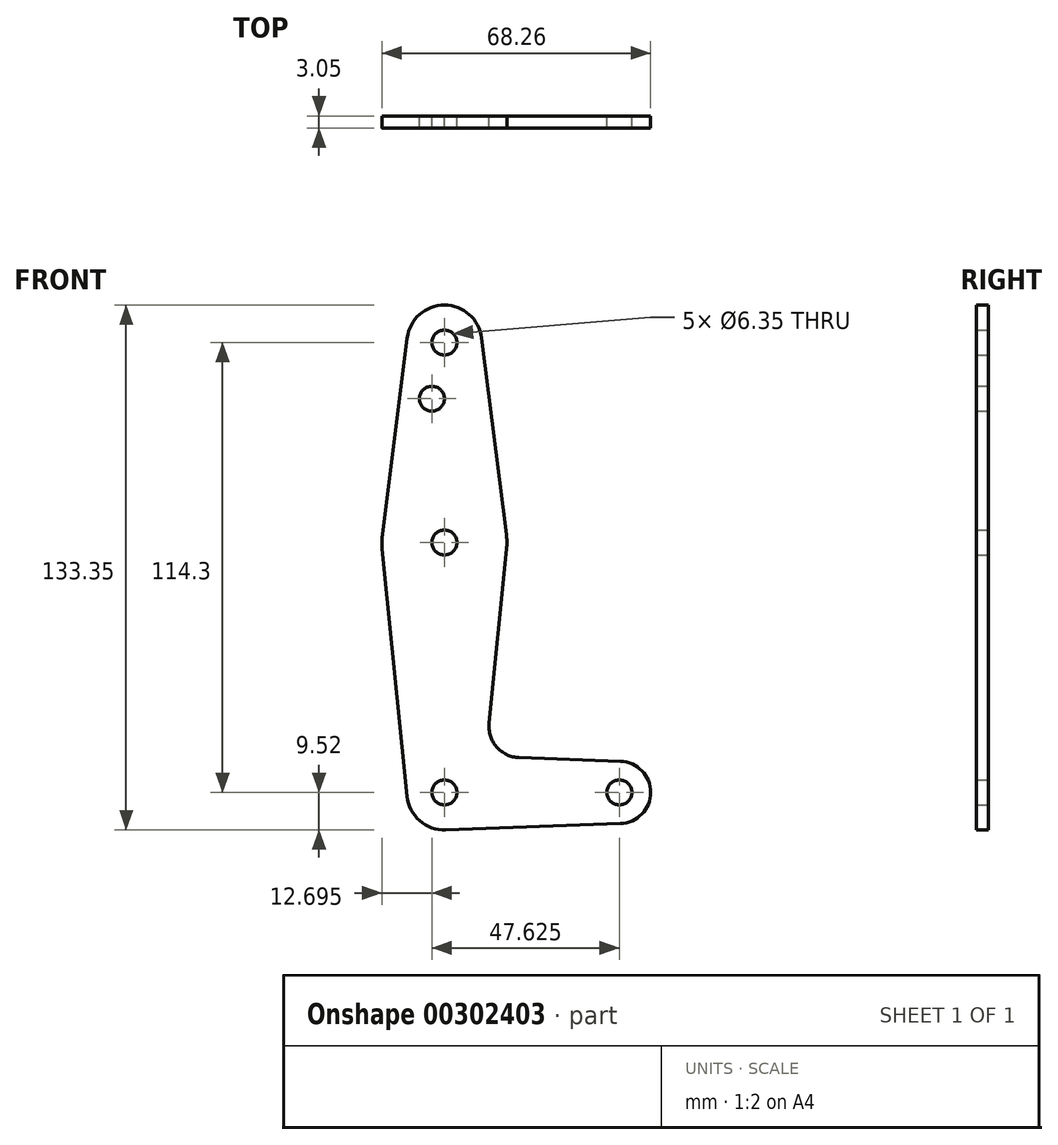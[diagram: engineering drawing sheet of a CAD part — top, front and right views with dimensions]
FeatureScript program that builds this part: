
annotation { "Feature Type Name" : "Feature", "Feature Type Description" : "" }
export const myFeature = defineFeature(function(context is Context, id is Id, definition is map)
    precondition{}
    {
        {
            var Q0;
            Q0=qCreatedBy(makeId("Front.planeOp"),FACE);
            var sketch = newSketch(context, id + "F0", { "sketchPlane" : qUnion([Q0])});
            skLineSegment(sketch, "E0", {"start": v(0, 0) * mm, "end": v(0, 114.3) * mm, "construction": true});
            skLineSegment(sketch, "E1", {"start": v(0, 0) * mm, "end": v(44.45, 0) * mm, "construction": true});
            skCircle(sketch, "E2", {"center": v(0, 114.3) * mm, "radius": 9.53 * mm});
            skCircle(sketch, "E3", {"center": v(0, 63.5) * mm, "radius": 15.88 * mm});
            skCircle(sketch, "E4", {"center": v(0, 0) * mm, "radius": 9.53 * mm});
            skCircle(sketch, "E5", {"center": v(44.45, 0) * mm, "radius": 7.94 * mm});
            skLineSegment(sketch, "E6", {"start": v(9.45, 115.5) * mm, "end": v(15.75, 65.48) * mm});
            skLineSegment(sketch, "E7", {"start": v(-15.8, 61.91) * mm, "end": v(-9.48, -0.95) * mm});
            skLineSegment(sketch, "E8", {"start": v(-9.45, 115.5) * mm, "end": v(-15.75, 65.48) * mm});
            skLineSegment(sketch, "E9", {"start": v(15.8, 61.91) * mm, "end": v(11.34, 17.6) * mm});
            skLineSegment(sketch, "E10", {"start": v(18.97, 8.85) * mm, "end": v(44.73, 7.93) * mm});
            skLineSegment(sketch, "E11", {"start": v(0.34, -9.52) * mm, "end": v(44.73, -7.93) * mm});
            skCircle(sketch, "E12", {"center": v(0, 114.3) * mm, "radius": 3.18 * mm});
            skCircle(sketch, "E13", {"center": v(0, 63.5) * mm, "radius": 3.18 * mm});
            skCircle(sketch, "E14", {"center": v(0, 0) * mm, "radius": 3.18 * mm});
            skCircle(sketch, "E15", {"center": v(44.45, 0) * mm, "radius": 3.18 * mm});
            skCircle(sketch, "E16", {"center": v(-3.18, 100.03) * mm, "radius": 3.18 * mm});
            skArc(sketch, "E17.filletArc", {"start": v(11.34, 17.6) * mm, "mid": v(13.26, 11.57) * mm, "end": v(18.97, 8.85) * mm});
            skSolve(sketch);
        }
        {
            var Q0;
            Q0=makeQuery(id+"F0.imprint","IMPRINT",FACE,{"disambiguationData":[TD([[makeQuery(id+"F0.imprint","IMPRINT",EDGE,{"derivedFrom":sQuery(id+"F0.wireOp",EDGE,"E12")}),-1.0]])]});
            var Q1;
            Q1=makeQuery(id+"F0.imprint","IMPRINT",FACE,{"disambiguationData":[TD([[makeQuery(id+"F0.imprint","IMPRINT",EDGE,{"derivedFrom":sQuery(id+"F0.wireOp",EDGE,"E14")}),-1.0]])]});
            var Q2;
            Q2=makeQuery(id+"F0.imprint","IMPRINT",FACE,{"disambiguationData":[TD([[makeQuery(id+"F0.imprint","IMPRINT",EDGE,{"derivedFrom":sQuery(id+"F0.wireOp",EDGE,"E15")}),-1.0]])]});
            var Q3;
            Q3=makeQuery(id+"F0.imprint","IMPRINT",FACE,{"disambiguationData":[TD([[makeQuery(id+"F0.imprint","IMPRINT",EDGE,{"derivedFrom":sQuery(id+"F0.wireOp",EDGE,"E13")}),-1.0]])]});
            var Q4;
            {var subQ0=sQuery(id+"F0.wireOp",EDGE,"E7");Q4=makeQuery(id+"F0.imprint","IMPRINT",FACE,{"disambiguationData":[TD([[makeQuery(id+"F0.imprint","IMPRINT",EDGE,{"derivedFrom":subQ0}),1.0]])]});}
            var Q5;
            {var subQ1=sQuery(id+"F0.wireOp",EDGE,"E6");Q5=makeQuery(id+"F0.imprint","IMPRINT",FACE,{"disambiguationData":[TD([[makeQuery(id+"F0.imprint","IMPRINT",EDGE,{"derivedFrom":subQ1}),-1.0]])]});}
            extrude(context, id + "F1", {"entities" : qUnion([Q0, Q1, Q2, Q3, Q4, Q5]), "depth" : 3.05 * mm});
        }
    });
